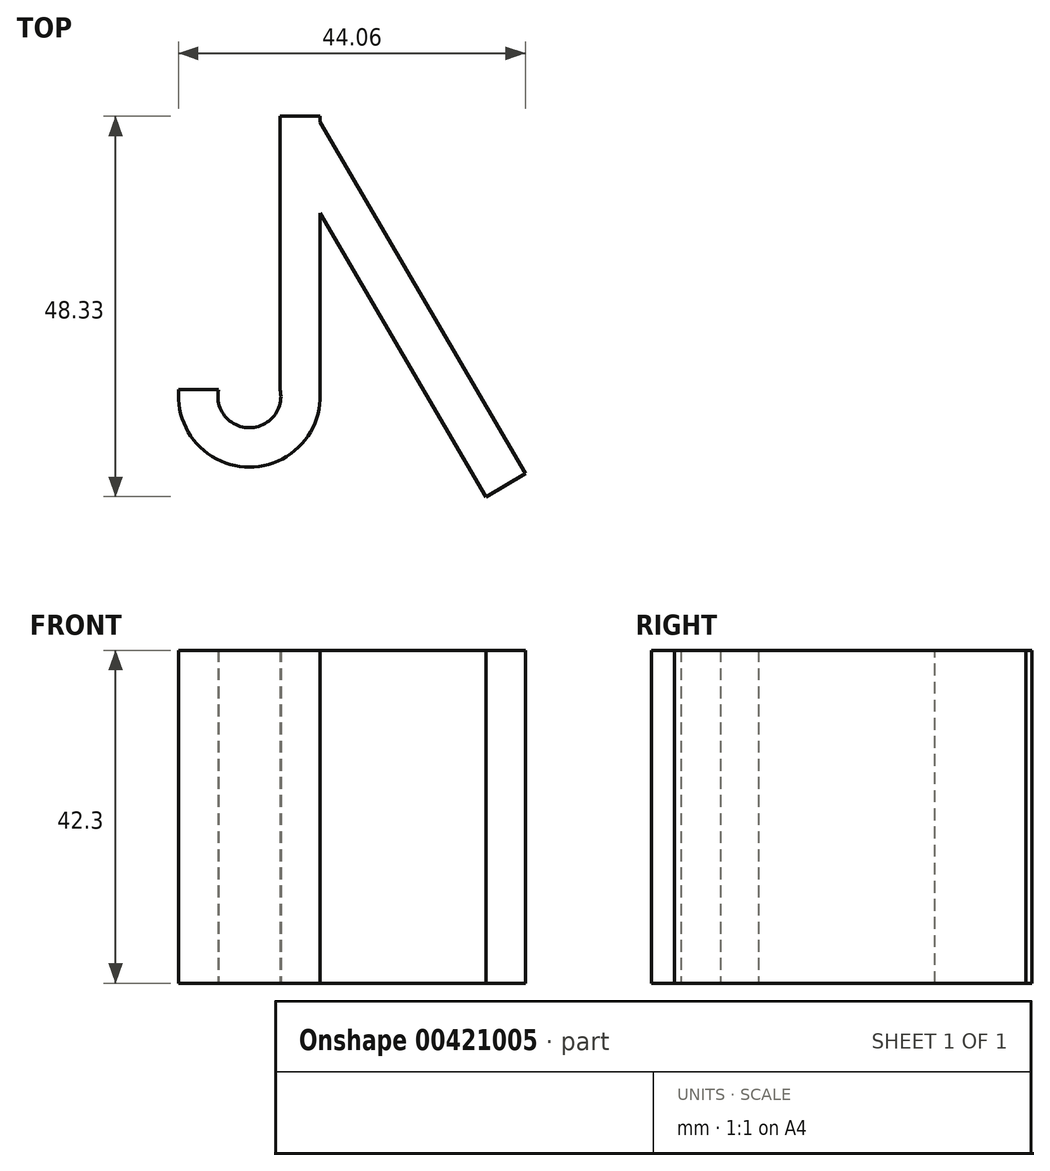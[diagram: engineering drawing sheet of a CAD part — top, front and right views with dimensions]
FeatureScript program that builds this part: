
annotation { "Feature Type Name" : "Feature", "Feature Type Description" : "" }
export const myFeature = defineFeature(function(context is Context, id is Id, definition is map)
    precondition{}
    {
        {
            var Q0;
            Q0=qCreatedBy(makeId("Top.planeOp"),FACE);
            var sketch = newSketch(context, id + "F0", { "sketchPlane" : qUnion([Q0])});
            skArc(sketch, "E0", {"start": v(-7.81, 0) * mm, "mid": v(-3.9, -4.86) * mm, "end": v(0, 0) * mm});
            skArc(sketch, "E1.0", {"start": v(-12.87, 0) * mm, "mid": v(-3.9, -9.86) * mm, "end": v(5.05, 0) * mm});
            skLineSegment(sketch, "E2", {"start": v(-12.87, 0) * mm, "end": v(-7.81, 0) * mm});
            skLineSegment(sketch, "E3", {"start": v(0, 0) * mm, "end": v(5.05, 0) * mm});
            skSolve(sketch);
        }
        {
            var Q0;
            Q0=sQuery(id+"F0.wireOp",EDGE,"E0");
            extrude(context, id + "F1", {"bodyType" : ToolBodyType.SURFACE, "surfaceEntities" : qUnion([Q0]), "depth" : 42.3 * mm});
        }
        {
            var Q0;
            Q0=sQuery(id+"F0.wireOp",EDGE,"E1.0");
            extrude(context, id + "F2", {"bodyType" : ToolBodyType.SURFACE, "surfaceEntities" : qUnion([Q0]), "depth" : 42.3 * mm});
        }
        {
            var Q0;
            Q0=makeQuery(id+"F0.imprint","IMPRINT",FACE,{"disambiguationData":[TD([[makeQuery(id+"F0.imprint","IMPRINT",EDGE,{"derivedFrom":sQuery(id+"F0.wireOp",EDGE,"E0")}),-1.0]])]});
            extrude(context, id + "F3", {"entities" : qUnion([Q0]), "depth" : 42.3 * mm});
        }
        {
            var Q0;
            Q0=makeQuery(id+"F3.opExtrude","SWEPT_FACE",FACE,{"disambiguationData":[OSD([sQuery(id+"F0.wireOp",EDGE,"E3")])]});
            var sketch = newSketch(context, id + "F4", { "sketchPlane" : qUnion([Q0])});
            skLineSegment(sketch, "E4", {"start": v(-5.05, 0) * mm, "end": v(-5.05, 42.3) * mm});
            skLineSegment(sketch, "E5", {"start": v(-5.05, 42.3) * mm, "end": v(0, 42.3) * mm});
            skLineSegment(sketch, "E6", {"start": v(0, 42.3) * mm, "end": v(0, 0) * mm});
            skLineSegment(sketch, "E7", {"start": v(0, 0) * mm, "end": v(-5.05, 0) * mm});
            skSolve(sketch);
        }
        {
            var Q0;
            Q0 = qSketchRegion(id + "F4", true);
            extrude(context, id + "F5", {"entities" : qUnion([Q0]), "operationType" : NewBodyOperationType.ADD, "depth" : 34.7 * mm});
        }
        {
            var Q0;
            Q0=qCreatedBy(makeId("Top.planeOp"),FACE);
            var sketch = newSketch(context, id + "F6", { "sketchPlane" : qUnion([Q0])});
            skLineSegment(sketch, "E8", {"start": v(4.74, 34.46) * mm, "end": v(31.15, -10.7) * mm});
            skLineSegment(sketch, "E9", {"start": v(31.15, -10.7) * mm, "end": v(26.13, -13.63) * mm});
            skLineSegment(sketch, "E10", {"start": v(26.13, -13.63) * mm, "end": v(4.67, 23.07) * mm});
            skLineSegment(sketch, "E11", {"start": v(4.67, 23.07) * mm, "end": v(4.74, 34.46) * mm});
            skSolve(sketch);
        }
        {
            var Q0;
            Q0 = qSketchRegion(id + "F6", true);
            extrude(context, id + "F7", {"entities" : qUnion([Q0]), "operationType" : NewBodyOperationType.ADD, "depth" : 42.3 * mm});
        }
    });
